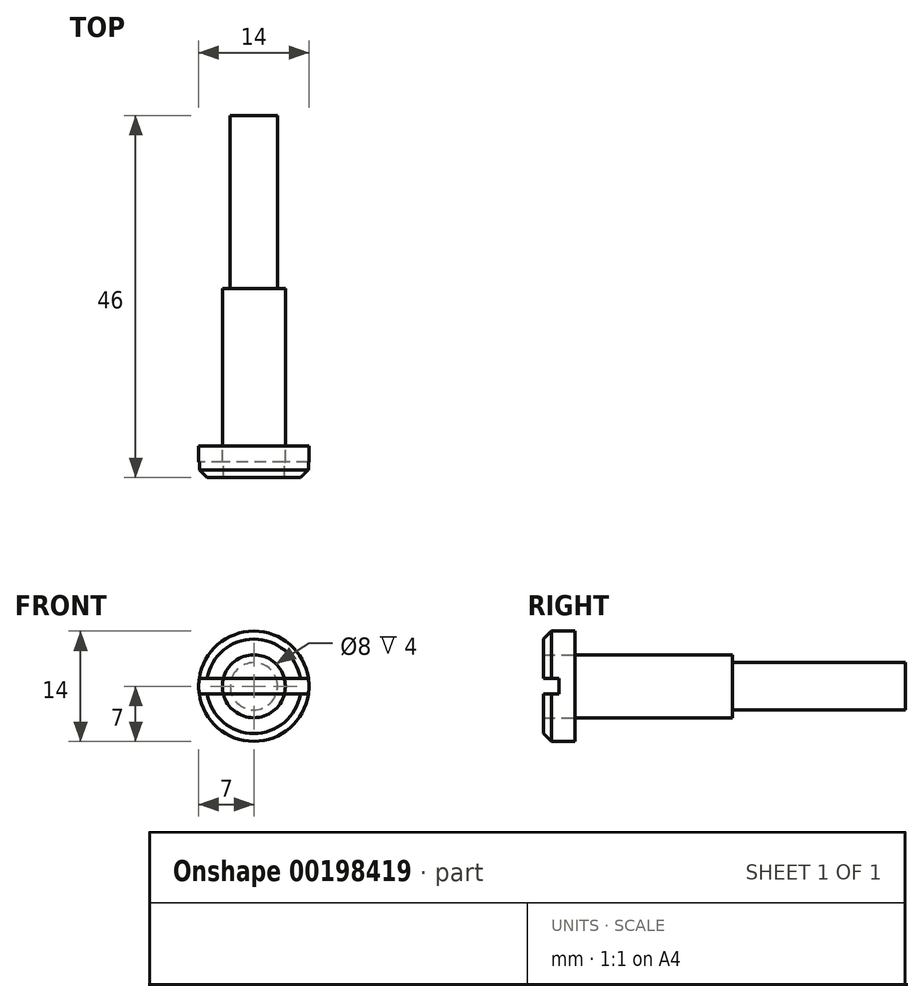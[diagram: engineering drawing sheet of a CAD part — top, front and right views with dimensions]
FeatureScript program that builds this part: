
annotation { "Feature Type Name" : "Feature", "Feature Type Description" : "" }
export const myFeature = defineFeature(function(context is Context, id is Id, definition is map)
    precondition{}
    {
        {
            var Q0;
            Q0=qCreatedBy(makeId("Front.planeOp"),FACE);
            var sketch = newSketch(context, id + "F0", { "sketchPlane" : qUnion([Q0])});
            skCircle(sketch, "E0", {"center": v(0, 0) * mm, "radius": 3 * mm});
            skCircle(sketch, "E1", {"center": v(0, 0) * mm, "radius": 4 * mm});
            skCircle(sketch, "E2", {"center": v(0, 0) * mm, "radius": 7 * mm});
            skSolve(sketch);
        }
        {
            var Q0;
            Q0=makeQuery(id+"F0.imprint","IMPRINT",FACE,{"disambiguationData":[TD([[makeQuery(id+"F0.imprint","IMPRINT",EDGE,{"derivedFrom":sQuery(id+"F0.wireOp",EDGE,"E0")}),1.0]])]});
            extrude(context, id + "F1", {"entities" : qUnion([Q0]), "oppositeDirection" : true, "depth" : 22 * mm, "hasSecondDirection" : true, "secondDirectionOppositeDirection" : false, "secondDirectionDepth" : 24 * mm});
        }
        {
            var Q0;
            Q0=makeQuery(id+"F0.imprint","IMPRINT",FACE,{"disambiguationData":[TD([[makeQuery(id+"F0.imprint","IMPRINT",EDGE,{"derivedFrom":sQuery(id+"F0.wireOp",EDGE,"E0")}),-1.0]])]});
            extrude(context, id + "F2", {"entities" : qUnion([Q0]), "operationType" : NewBodyOperationType.ADD, "depth" : 24 * mm});
        }
        {
            var Q0;
            Q0=makeQuery(id+"F0.imprint","IMPRINT",FACE,{"disambiguationData":[TD([[makeQuery(id+"F0.imprint","IMPRINT",EDGE,{"derivedFrom":sQuery(id+"F0.wireOp",EDGE,"E1")}),-1.0]])]});
            extrude(context, id + "F3", {"entities" : qUnion([Q0]), "depth" : 24 * mm, "hasSecondDirection" : true, "secondDirectionOppositeDirection" : false, "secondDirectionDepth" : 20 * mm});
        }
        {
            var Q0;
            Q0=qCreatedBy(makeId("Front.planeOp"),FACE);
            var sketch = newSketch(context, id + "F4", { "sketchPlane" : qUnion([Q0])});
            skLineSegment(sketch, "E3.bottom", {"start": v(15, -1) * mm, "end": v(-15, -1) * mm});
            skLineSegment(sketch, "E3.top", {"start": v(15, 1) * mm, "end": v(-15, 1) * mm});
            skLineSegment(sketch, "E3.left", {"start": v(15, -1) * mm, "end": v(15, 1) * mm});
            skLineSegment(sketch, "E3.right", {"start": v(-15, -1) * mm, "end": v(-15, 1) * mm});
            skPoint(sketch, "E3.middle", {"position": v(0, 0) * mm});
            skSolve(sketch);
        }
        {
            var Q0;
            Q0 = qSketchRegion(id + "F4", true);
            extrude(context, id + "F5", {"entities" : qUnion([Q0]), "operationType" : NewBodyOperationType.REMOVE, "depth" : 25 * mm, "hasSecondDirection" : true, "secondDirectionOppositeDirection" : false, "secondDirectionDepth" : 22 * mm});
        }
        {
            var Q0;
            {var subQ2=sQuery(id+"F0.wireOp",EDGE,"E2");Q0=makeQuery(id+"F5.boolean.opBoolean","SPLIT",EDGE,{"disambiguationData":[TD([makeQuery(id+"F5.opExtrude","SWEPT_FACE",FACE,{"disambiguationData":[OSD([sQuery(id+"F4.wireOp",EDGE,"E3.top")])]})])],"derivedFrom":makeQuery(id+"F3.opExtrude","CAP_EDGE",EDGE,{"disambiguationData":[OSD([subQ2])],"isStart":false})});}
            var Q1;
            {var subQ2=sQuery(id+"F0.wireOp",EDGE,"E2");Q1=makeQuery(id+"F5.boolean.opBoolean","SPLIT",EDGE,{"disambiguationData":[TD([makeQuery(id+"F5.opExtrude","SWEPT_FACE",FACE,{"disambiguationData":[OSD([sQuery(id+"F4.wireOp",EDGE,"E3.bottom")])]})])],"derivedFrom":makeQuery(id+"F3.opExtrude","CAP_EDGE",EDGE,{"disambiguationData":[OSD([subQ2])],"isStart":false})});}
            chamfer(context, id + "F6", {"entities" : qUnion([Q0, Q1]), "width" : 1 * mm, "tangentPropagation" : true});
        }
    });
